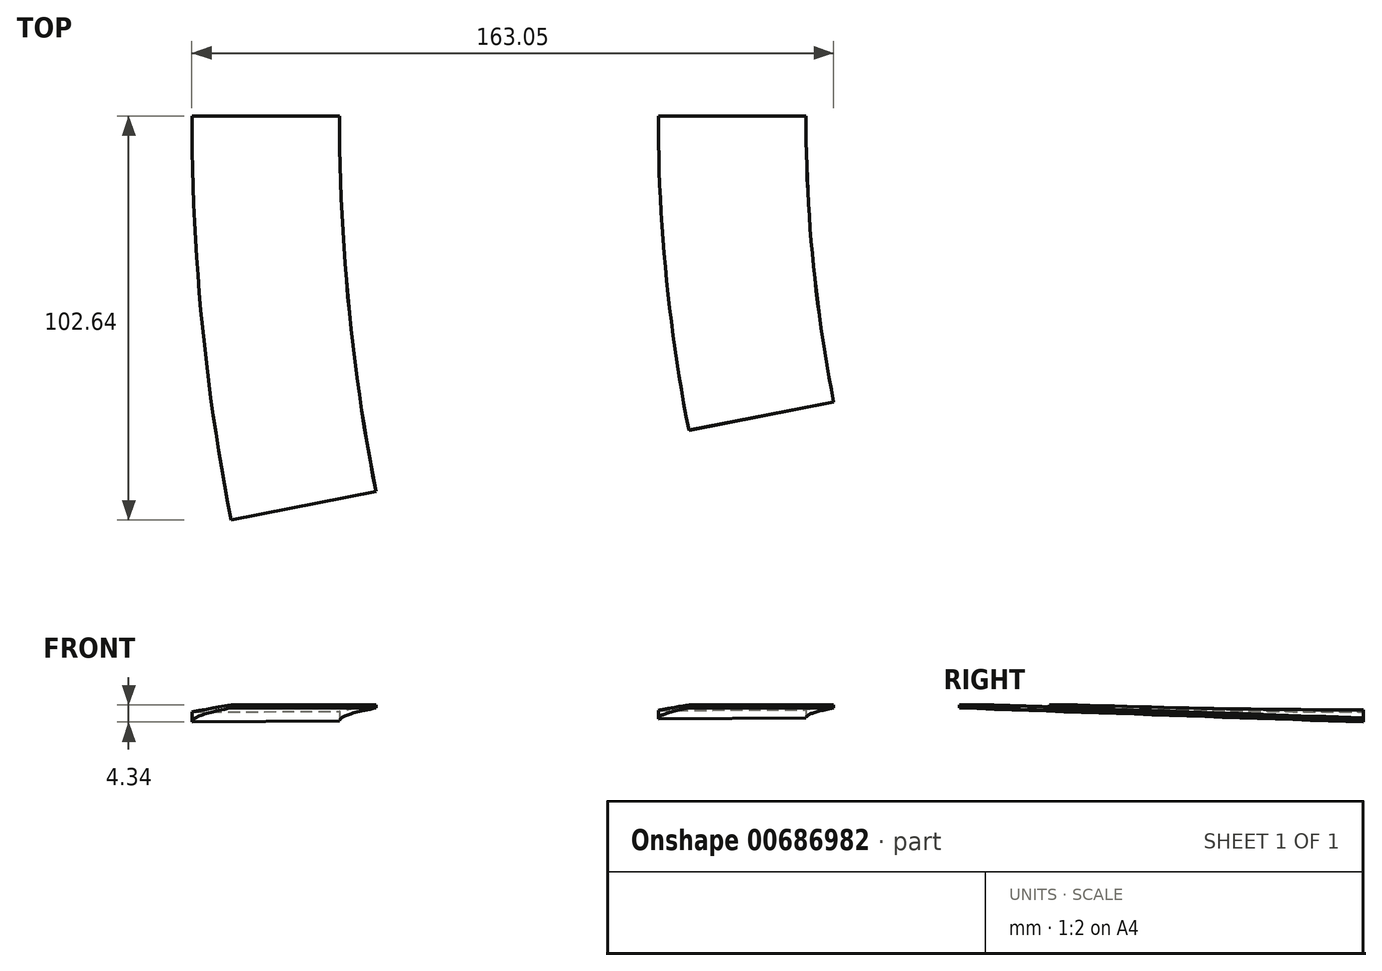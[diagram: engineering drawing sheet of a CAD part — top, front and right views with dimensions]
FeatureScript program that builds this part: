
annotation { "Feature Type Name" : "Feature", "Feature Type Description" : "" }
export const myFeature = defineFeature(function(context is Context, id is Id, definition is map)
    precondition{}
    {
        {
            var Q0;
            Q0=qCreatedBy(makeId("Front.planeOp"),FACE);
            var sketch = newSketch(context, id + "F0", { "sketchPlane" : qUnion([Q0])});
            skLineSegment(sketch, "E0", {"start": v(-0.07, -1.79) * mm, "end": v(534.04, 0) * mm});
            skLineSegment(sketch, "E1", {"start": v(534.04, 0) * mm, "end": v(517.63, 91.28) * mm});
            skLineSegment(sketch, "E2", {"start": v(517.63, 91.28) * mm, "end": v(-0.07, -1.79) * mm});
            skLineSegment(sketch, "E3", {"start": v(517.63, 91.28) * mm, "end": v(483.66, 280.23) * mm});
            skLineSegment(sketch, "E4", {"start": v(483.66, 280.23) * mm, "end": v(-34.04, 187.15) * mm});
            skArc(sketch, "E5", {"start": v(-34.04, 187.15) * mm, "mid": v(-22.42, 136.86) * mm, "end": v(-5.93, 87.94) * mm});
            skLineSegment(sketch, "E6", {"start": v(-5.93, 87.94) * mm, "end": v(483.66, 280.23) * mm});
            skLineSegment(sketch, "E7", {"start": v(-5.93, 87.94) * mm, "end": v(9.88, 0) * mm});
            skLineSegment(sketch, "E8", {"start": v(-0.07, -1.79) * mm, "end": v(0, -21.79) * mm});
            skLineSegment(sketch, "E9", {"start": v(0, -21.79) * mm, "end": v(156, -21.27) * mm});
            skLineSegment(sketch, "E10", {"start": v(156, -21.27) * mm, "end": v(155.93, -1.27) * mm});
            skLineSegment(sketch, "E11", {"start": v(118.43, -1.4) * mm, "end": v(118.5, -21.4) * mm});
            skLineSegment(sketch, "E12", {"start": v(37.43, -1.66) * mm, "end": v(37.5, -21.66) * mm});
            skSolve(sketch);
        }
        {
            var Q0;
            {var subQ0=sQuery(id+"F0.wireOp",EDGE,"E8");Q0=makeQuery(id+"F0.imprint","IMPRINT",FACE,{"disambiguationData":[TD([[makeQuery(id+"F0.imprint","IMPRINT",EDGE,{"derivedFrom":subQ0}),1.0]])]});}
            var Q1;
            {var subQ0=sQuery(id+"F0.wireOp",EDGE,"E10");Q1=makeQuery(id+"F0.imprint","IMPRINT",FACE,{"disambiguationData":[TD([[makeQuery(id+"F0.imprint","IMPRINT",EDGE,{"derivedFrom":subQ0}),1.0]])]});}
            var Q2;
            Q2=sQuery(id+"F0.wireOp",EDGE,"E1");
            revolve(context, id + "F1", {"entities" : qUnion([Q0, Q1]), "axis" : qUnion([Q2]), "revolveType" : RevolveType.SYMMETRIC, "angle" : 22.5 * degree});
        }
        {
            var Q0;
            Q0=qCreatedBy(makeId("Front.planeOp"),FACE);
            var sketch = newSketch(context, id + "F2", { "sketchPlane" : qUnion([Q0])});
            skLineSegment(sketch, "E13.bottom", {"start": v(-11.76, -6.8) * mm, "end": v(174.62, -6.8) * mm});
            skLineSegment(sketch, "E13.top", {"start": v(-11.76, -27.47) * mm, "end": v(174.62, -27.47) * mm});
            skLineSegment(sketch, "E13.left", {"start": v(-11.76, -6.8) * mm, "end": v(-11.76, -27.47) * mm});
            skLineSegment(sketch, "E13.right", {"start": v(174.62, -6.8) * mm, "end": v(174.62, -27.47) * mm});
            skSolve(sketch);
        }
        {
            var Q0;
            Q0=makeQuery(id+"F2.imprint","IMPRINT",FACE,{"disambiguationData":[TD([[makeQuery(id+"F2.imprint","IMPRINT",EDGE,{"derivedFrom":sQuery(id+"F2.wireOp",EDGE,"E13.bottom")}),-1.0]])]});
            extrude(context, id + "F3", {"entities" : qUnion([Q0]), "operationType" : NewBodyOperationType.REMOVE, "endBound" : BoundingType.SYMMETRIC, "depth" : 236.2 * mm, "offsetDistance" : 25 * mm});
        }
        {
            var Q0;
            Q0=makeQuery(id+"F1.opRevolve","CAP_FACE",FACE,{"disambiguationData":[OSD([sQuery(id+"F0.wireOp",EDGE,"E0"),sQuery(id+"F0.wireOp",EDGE,"E9"),sQuery(id+"F0.wireOp",EDGE,"E10"),sQuery(id+"F0.wireOp",EDGE,"E11")])],"isStart":false});
            var sketch = newSketch(context, id + "F4", { "sketchPlane" : qUnion([Q0])});
            skLineSegment(sketch, "E14", {"start": v(103.7, -3.64) * mm, "end": v(181.28, -3.12) * mm});
            skLineSegment(sketch, "E15", {"start": v(181.28, -3.12) * mm, "end": v(182.29, -19.2) * mm});
            skLineSegment(sketch, "E16", {"start": v(182.29, -19.2) * mm, "end": v(102.35, -20.5) * mm});
            skLineSegment(sketch, "E17", {"start": v(102.35, -20.5) * mm, "end": v(103.7, -3.64) * mm});
            skSolve(sketch);
        }
        {
            var Q0;
            {var subQ0=sQuery(id+"F4.wireOp",EDGE,"E15");Q0=makeQuery(id+"F4.imprint","IMPRINT",FACE,{"disambiguationData":[TD([[makeQuery(id+"F4.imprint","IMPRINT",EDGE,{"derivedFrom":subQ0}),-1.0]])]});}
            var Q1;
            {var subQ0=sQuery(id+"F4.wireOp",EDGE,"E14");var subQ1=sQuery(id+"F0.wireOp",EDGE,"E11");var subQ2=makeQuery(id+"F1.opRevolve","CAP_EDGE",EDGE,{"disambiguationData":[OSD([subQ1])],"isStart":false});var subQ3=makeQuery(id+"F4.imprint","INTERSECT",VERTEX,{"derivedFrom":[subQ2,subQ0]});Q1=makeQuery(id+"F4.imprint","IMPRINT",FACE,{"disambiguationData":[TD([[makeQuery(id+"F4.imprint","IMPRINT",EDGE,{"disambiguationData":[TD([[subQ3,-1.0]])],"derivedFrom":subQ0}),-1.0]])]});}
            extrude(context, id + "F5", {"entities" : qUnion([Q0, Q1]), "operationType" : NewBodyOperationType.REMOVE, "oppositeDirection" : true, "depth" : 202.1 * mm, "offsetDistance" : 25 * mm});
        }
        {
            var Q0;
            Q0=makeQuery(id+"F1.opRevolve","CAP_FACE",FACE,{"disambiguationData":[OSD([sQuery(id+"F0.wireOp",EDGE,"E0"),sQuery(id+"F0.wireOp",EDGE,"E8"),sQuery(id+"F0.wireOp",EDGE,"E9"),sQuery(id+"F0.wireOp",EDGE,"E12")])],"isStart":false});
            var sketch = newSketch(context, id + "F6", { "sketchPlane" : qUnion([Q0])});
            skLineSegment(sketch, "E18", {"start": v(-32.8, -4.56) * mm, "end": v(69.34, -3.87) * mm});
            skLineSegment(sketch, "E19", {"start": v(69.34, -3.87) * mm, "end": v(68.29, -26.31) * mm});
            skLineSegment(sketch, "E20", {"start": v(68.29, -26.31) * mm, "end": v(-31.65, -34.3) * mm});
            skLineSegment(sketch, "E21", {"start": v(-31.65, -34.3) * mm, "end": v(-32.8, -4.56) * mm});
            skSolve(sketch);
        }
        {
            var Q0;
            {var subQ0=sQuery(id+"F6.wireOp",EDGE,"E19");Q0=makeQuery(id+"F6.imprint","IMPRINT",FACE,{"disambiguationData":[TD([[makeQuery(id+"F6.imprint","IMPRINT",EDGE,{"derivedFrom":subQ0}),-1.0]])]});}
            var Q1;
            {var subQ0=sQuery(id+"F6.wireOp",EDGE,"E18");var subQ1=sQuery(id+"F0.wireOp",EDGE,"E8");var subQ2=makeQuery(id+"F1.opRevolve","CAP_EDGE",EDGE,{"disambiguationData":[OSD([subQ1])],"isStart":false});var subQ3=makeQuery(id+"F6.imprint","INTERSECT",VERTEX,{"derivedFrom":[subQ2,subQ0]});Q1=makeQuery(id+"F6.imprint","IMPRINT",FACE,{"disambiguationData":[TD([[makeQuery(id+"F6.imprint","IMPRINT",EDGE,{"disambiguationData":[TD([[subQ3,-1.0]])],"derivedFrom":subQ0}),-1.0]])]});}
            extrude(context, id + "F7", {"entities" : qUnion([Q0, Q1]), "operationType" : NewBodyOperationType.REMOVE, "oppositeDirection" : true, "depth" : 395.5 * mm, "offsetDistance" : 25 * mm});
        }
        {
            var Q0;
            Q0=qCreatedBy(makeId("Front.planeOp"),FACE);
            var sketch = newSketch(context, id + "F8", { "sketchPlane" : qUnion([Q0])});
            skLineSegment(sketch, "E22.bottom", {"start": v(208.28, 68.13) * mm, "end": v(-87.57, 68.13) * mm});
            skLineSegment(sketch, "E22.top", {"start": v(208.28, -89.62) * mm, "end": v(-87.57, -89.62) * mm});
            skLineSegment(sketch, "E22.left", {"start": v(208.28, 68.13) * mm, "end": v(208.28, -89.62) * mm});
            skLineSegment(sketch, "E22.right", {"start": v(-87.57, 68.13) * mm, "end": v(-87.57, -89.62) * mm});
            skSolve(sketch);
        }
        {
            var Q0;
            Q0=makeQuery(id+"F8.imprint","IMPRINT",FACE,{"disambiguationData":[TD([[makeQuery(id+"F8.imprint","IMPRINT",EDGE,{"derivedFrom":sQuery(id+"F8.wireOp",EDGE,"E22.bottom")}),1.0]])]});
            extrude(context, id + "F9", {"entities" : qUnion([Q0]), "operationType" : NewBodyOperationType.REMOVE, "oppositeDirection" : true, "depth" : 233 * mm, "offsetDistance" : 25 * mm});
        }
    });
